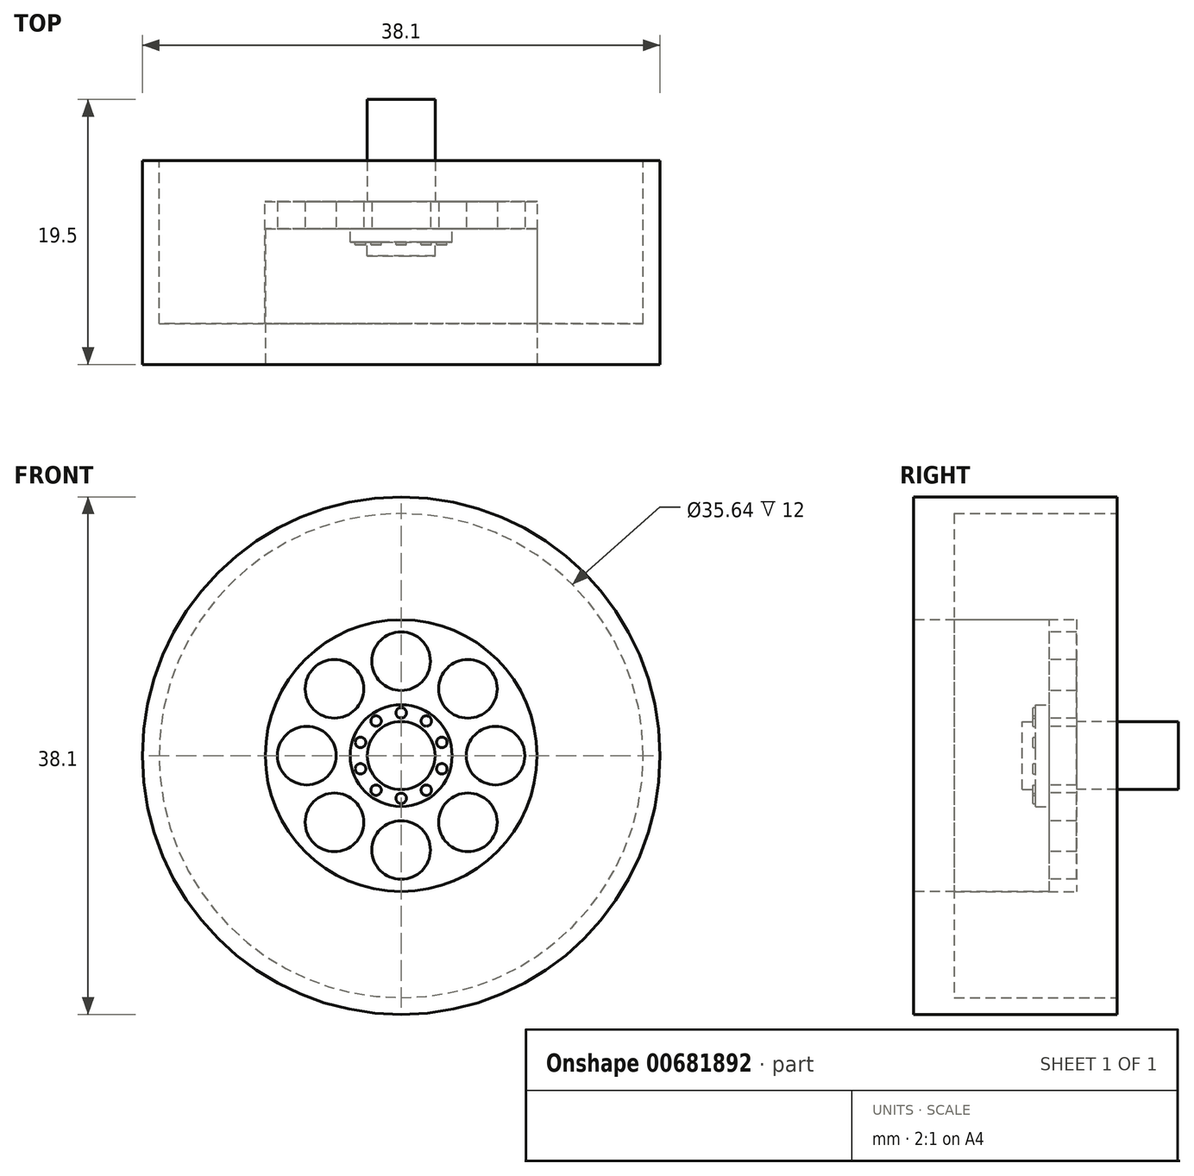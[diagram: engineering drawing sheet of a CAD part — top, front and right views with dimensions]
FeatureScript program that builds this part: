
annotation { "Feature Type Name" : "Feature", "Feature Type Description" : "" }
export const myFeature = defineFeature(function(context is Context, id is Id, definition is map)
    precondition{}
    {
        {
            var Q0;
            Q0=qCreatedBy(makeId("Front.planeOp"),FACE);
            var sketch = newSketch(context, id + "F0", { "sketchPlane" : qUnion([Q0])});
            skCircle(sketch, "E0", {"center": v(0, 0) * mm, "radius": 19.05 * mm});
            skSolve(sketch);
        }
        {
            var Q0;
            Q0=makeQuery(id+"F0.imprint","IMPRINT",FACE,{"disambiguationData":[TD([[makeQuery(id+"F0.imprint","IMPRINT",EDGE,{"derivedFrom":sQuery(id+"F0.wireOp",EDGE,"E0")}),1.0]])]});
            extrude(context, id + "F1", {"entities" : qUnion([Q0]), "depth" : 15 * mm, "offsetDistance" : 25.4 * mm});
        }
        {
            var Q0;
            Q0=makeQuery(id+"F1.opExtrude","CAP_FACE",FACE,{"disambiguationData":[OSD([sQuery(id+"F0.wireOp",EDGE,"E0")])],"isStart":false});
            var sketch = newSketch(context, id + "F2", { "sketchPlane" : qUnion([Q0])});
            skCircle(sketch, "E1", {"center": v(0, 0) * mm, "radius": 10 * mm});
            skSolve(sketch);
        }
        {
            var Q0;
            Q0=makeQuery(id+"F2.imprint","IMPRINT",FACE,{"disambiguationData":[TD([[makeQuery(id+"F2.imprint","IMPRINT",EDGE,{"derivedFrom":sQuery(id+"F2.wireOp",EDGE,"E1")}),1.0]])]});
            extrude(context, id + "F3", {"entities" : qUnion([Q0]), "operationType" : NewBodyOperationType.REMOVE, "oppositeDirection" : true, "depth" : 10 * mm, "offsetDistance" : 25.4 * mm});
        }
        {
            var Q0;
            Q0=makeQuery(id+"F3.boolean.opBoolean","COPY",FACE,{"derivedFrom":makeQuery(id+"F3.opExtrude","CAP_FACE",FACE,{"disambiguationData":[OSD([sQuery(id+"F2.wireOp",EDGE,"E1")])],"isStart":false})});
            var sketch = newSketch(context, id + "F4", { "sketchPlane" : qUnion([Q0])});
            skCircle(sketch, "E2", {"center": v(0, 0) * mm, "radius": 3.75 * mm});
            skSolve(sketch);
        }
        {
            var Q0;
            Q0=makeQuery(id+"F4.imprint","IMPRINT",FACE,{"disambiguationData":[TD([[makeQuery(id+"F4.imprint","IMPRINT",EDGE,{"derivedFrom":sQuery(id+"F4.wireOp",EDGE,"E2")}),1.0]])]});
            extrude(context, id + "F5", {"entities" : qUnion([Q0]), "operationType" : NewBodyOperationType.ADD, "depth" : 1 * mm, "offsetDistance" : 25.4 * mm});
        }
        {
            var Q0;
            Q0=makeQuery(id+"F5.opExtrude","CAP_FACE",FACE,{"disambiguationData":[OSD([sQuery(id+"F4.wireOp",EDGE,"E2")])],"isStart":false});
            var sketch = newSketch(context, id + "F6", { "sketchPlane" : qUnion([Q0])});
            skCircle(sketch, "E3", {"center": v(0, 0) * mm, "radius": 2.5 * mm});
            skSolve(sketch);
        }
        {
            var Q0;
            Q0=makeQuery(id+"F6.imprint","IMPRINT",FACE,{"disambiguationData":[TD([[makeQuery(id+"F6.imprint","IMPRINT",EDGE,{"derivedFrom":sQuery(id+"F6.wireOp",EDGE,"E3")}),1.0]])]});
            extrude(context, id + "F7", {"entities" : qUnion([Q0]), "operationType" : NewBodyOperationType.ADD, "depth" : 1 * mm, "offsetDistance" : 25.4 * mm});
        }
        {
            var Q0;
            Q0=makeQuery(id+"F3.boolean.opBoolean","COPY",FACE,{"derivedFrom":makeQuery(id+"F3.opExtrude","CAP_FACE",FACE,{"disambiguationData":[OSD([sQuery(id+"F2.wireOp",EDGE,"E1")])],"isStart":false})});
            var sketch = newSketch(context, id + "F8", { "sketchPlane" : qUnion([Q0])});
            skCircle(sketch, "E4", {"center": v(0, 6.95) * mm, "radius": 2.16 * mm});
            skCircle(sketch, "E5.1.0", {"center": v(-4.91, 4.91) * mm, "radius": 2.16 * mm});
            skCircle(sketch, "E5.2.0", {"center": v(-6.95, 0) * mm, "radius": 2.16 * mm});
            skCircle(sketch, "E5.3.0", {"center": v(-4.91, -4.91) * mm, "radius": 2.16 * mm});
            skCircle(sketch, "E5.4.0", {"center": v(0, -6.95) * mm, "radius": 2.16 * mm});
            skCircle(sketch, "E5.5.0", {"center": v(4.91, -4.91) * mm, "radius": 2.16 * mm});
            skCircle(sketch, "E5.6.0", {"center": v(6.95, 0) * mm, "radius": 2.16 * mm});
            skCircle(sketch, "E5.7.0", {"center": v(4.91, 4.91) * mm, "radius": 2.16 * mm});
            skPoint(sketch, "E5.center", {"position": v(0, 0) * mm});
            skSolve(sketch);
        }
        {
            var Q0;
            Q0=makeQuery(id+"F8.imprint","IMPRINT",FACE,{"disambiguationData":[TD([[makeQuery(id+"F8.imprint","IMPRINT",EDGE,{"derivedFrom":sQuery(id+"F8.wireOp",EDGE,"E4")}),1.0]])]});
            var Q1;
            Q1=makeQuery(id+"F8.imprint","IMPRINT",FACE,{"disambiguationData":[TD([[makeQuery(id+"F8.imprint","IMPRINT",EDGE,{"derivedFrom":sQuery(id+"F8.wireOp",EDGE,"E5.7.0")}),1.0]])]});
            var Q2;
            Q2=makeQuery(id+"F8.imprint","IMPRINT",FACE,{"disambiguationData":[TD([[makeQuery(id+"F8.imprint","IMPRINT",EDGE,{"derivedFrom":sQuery(id+"F8.wireOp",EDGE,"E5.6.0")}),1.0]])]});
            var Q3;
            Q3=makeQuery(id+"F8.imprint","IMPRINT",FACE,{"disambiguationData":[TD([[makeQuery(id+"F8.imprint","IMPRINT",EDGE,{"derivedFrom":sQuery(id+"F8.wireOp",EDGE,"E5.5.0")}),1.0]])]});
            var Q4;
            Q4=makeQuery(id+"F8.imprint","IMPRINT",FACE,{"disambiguationData":[TD([[makeQuery(id+"F8.imprint","IMPRINT",EDGE,{"derivedFrom":sQuery(id+"F8.wireOp",EDGE,"E5.4.0")}),1.0]])]});
            var Q5;
            Q5=makeQuery(id+"F8.imprint","IMPRINT",FACE,{"disambiguationData":[TD([[makeQuery(id+"F8.imprint","IMPRINT",EDGE,{"derivedFrom":sQuery(id+"F8.wireOp",EDGE,"E5.3.0")}),1.0]])]});
            var Q6;
            Q6=makeQuery(id+"F8.imprint","IMPRINT",FACE,{"disambiguationData":[TD([[makeQuery(id+"F8.imprint","IMPRINT",EDGE,{"derivedFrom":sQuery(id+"F8.wireOp",EDGE,"E5.2.0")}),1.0]])]});
            var Q7;
            Q7=makeQuery(id+"F8.imprint","IMPRINT",FACE,{"disambiguationData":[TD([[makeQuery(id+"F8.imprint","IMPRINT",EDGE,{"derivedFrom":sQuery(id+"F8.wireOp",EDGE,"E5.1.0")}),1.0]])]});
            extrude(context, id + "F9", {"entities" : qUnion([Q0, Q1, Q2, Q3, Q4, Q5, Q6, Q7]), "operationType" : NewBodyOperationType.REMOVE, "oppositeDirection" : true, "depth" : 18.8 * mm, "offsetDistance" : 25.4 * mm});
        }
        {
            var Q0;
            Q0=makeQuery(id+"F1.opExtrude","CAP_FACE",FACE,{"disambiguationData":[OSD([sQuery(id+"F0.wireOp",EDGE,"E0")])],"isStart":true});
            var sketch = newSketch(context, id + "F10", { "sketchPlane" : qUnion([Q0])});
            skCircle(sketch, "E6", {"center": v(0, 0) * mm, "radius": 17.5 * mm});
            skSolve(sketch);
        }
        {
            var Q0;
            Q0=makeQuery(id+"F10.imprint","IMPRINT",FACE,{"disambiguationData":[TD([[makeQuery(id+"F10.imprint","IMPRINT",EDGE,{"derivedFrom":sQuery(id+"F10.wireOp",EDGE,"E6")}),1.0]])]});
            extrude(context, id + "F11", {"entities" : qUnion([Q0]), "operationType" : NewBodyOperationType.REMOVE, "oppositeDirection" : true, "depth" : 3 * mm, "offsetDistance" : 25.4 * mm});
        }
        {
            var Q0;
            Q0=makeQuery(id+"F11.boolean.opBoolean","COPY",FACE,{"derivedFrom":makeQuery(id+"F11.opExtrude","CAP_FACE",FACE,{"disambiguationData":[OSD([sQuery(id+"F0.wireOp",EDGE,"E0"),sQuery(id+"F8.wireOp",EDGE,"E4"),sQuery(id+"F8.wireOp",EDGE,"E5.1.0"),sQuery(id+"F8.wireOp",EDGE,"E5.2.0"),sQuery(id+"F8.wireOp",EDGE,"E5.3.0"),sQuery(id+"F8.wireOp",EDGE,"E5.4.0"),sQuery(id+"F8.wireOp",EDGE,"E5.5.0"),sQuery(id+"F8.wireOp",EDGE,"E5.6.0"),sQuery(id+"F8.wireOp",EDGE,"E5.7.0"),sQuery(id+"F10.wireOp",EDGE,"E6")])],"isStart":false})});
            var sketch = newSketch(context, id + "F12", { "sketchPlane" : qUnion([Q0])});
            skCircle(sketch, "E7", {"center": v(0, 0) * mm, "radius": 2.5 * mm});
            skSolve(sketch);
        }
        {
            var Q0;
            Q0=makeQuery(id+"F5.opExtrude","CAP_FACE",FACE,{"disambiguationData":[OSD([sQuery(id+"F4.wireOp",EDGE,"E2")])],"isStart":false});
            var sketch = newSketch(context, id + "F13", { "sketchPlane" : qUnion([Q0])});
            skCircle(sketch, "E8", {"center": v(0, 3.15) * mm, "radius": 0.39 * mm});
            skCircle(sketch, "E9.1.0", {"center": v(-1.85, 2.55) * mm, "radius": 0.39 * mm});
            skCircle(sketch, "E9.2.0", {"center": v(-3, 0.97) * mm, "radius": 0.39 * mm});
            skCircle(sketch, "E9.3.0", {"center": v(-3, -0.97) * mm, "radius": 0.39 * mm});
            skCircle(sketch, "E9.4.0", {"center": v(-1.85, -2.55) * mm, "radius": 0.39 * mm});
            skCircle(sketch, "E9.5.0", {"center": v(0, -3.15) * mm, "radius": 0.39 * mm});
            skCircle(sketch, "E9.6.0", {"center": v(1.85, -2.55) * mm, "radius": 0.39 * mm});
            skCircle(sketch, "E9.7.0", {"center": v(3, -0.97) * mm, "radius": 0.39 * mm});
            skCircle(sketch, "E9.8.0", {"center": v(3, 0.97) * mm, "radius": 0.39 * mm});
            skCircle(sketch, "E9.9.0", {"center": v(1.85, 2.55) * mm, "radius": 0.39 * mm});
            skPoint(sketch, "E9.center", {"position": v(0, 0) * mm});
            skSolve(sketch);
        }
        {
            var Q0;
            Q0=makeQuery(id+"F13.imprint","IMPRINT",FACE,{"disambiguationData":[TD([[makeQuery(id+"F13.imprint","IMPRINT",EDGE,{"derivedFrom":sQuery(id+"F13.wireOp",EDGE,"E8")}),1.0]])]});
            var Q1;
            Q1=makeQuery(id+"F13.imprint","IMPRINT",FACE,{"disambiguationData":[TD([[makeQuery(id+"F13.imprint","IMPRINT",EDGE,{"derivedFrom":sQuery(id+"F13.wireOp",EDGE,"E9.9.0")}),1.0]])]});
            var Q2;
            Q2=makeQuery(id+"F13.imprint","IMPRINT",FACE,{"disambiguationData":[TD([[makeQuery(id+"F13.imprint","IMPRINT",EDGE,{"derivedFrom":sQuery(id+"F13.wireOp",EDGE,"E9.8.0")}),1.0]])]});
            var Q3;
            Q3=makeQuery(id+"F13.imprint","IMPRINT",FACE,{"disambiguationData":[TD([[makeQuery(id+"F13.imprint","IMPRINT",EDGE,{"derivedFrom":sQuery(id+"F13.wireOp",EDGE,"E9.7.0")}),1.0]])]});
            var Q4;
            Q4=makeQuery(id+"F13.imprint","IMPRINT",FACE,{"disambiguationData":[TD([[makeQuery(id+"F13.imprint","IMPRINT",EDGE,{"derivedFrom":sQuery(id+"F13.wireOp",EDGE,"E9.6.0")}),1.0]])]});
            var Q5;
            Q5=makeQuery(id+"F13.imprint","IMPRINT",FACE,{"disambiguationData":[TD([[makeQuery(id+"F13.imprint","IMPRINT",EDGE,{"derivedFrom":sQuery(id+"F13.wireOp",EDGE,"E9.5.0")}),1.0]])]});
            var Q6;
            Q6=makeQuery(id+"F13.imprint","IMPRINT",FACE,{"disambiguationData":[TD([[makeQuery(id+"F13.imprint","IMPRINT",EDGE,{"derivedFrom":sQuery(id+"F13.wireOp",EDGE,"E9.4.0")}),1.0]])]});
            var Q7;
            Q7=makeQuery(id+"F13.imprint","IMPRINT",FACE,{"disambiguationData":[TD([[makeQuery(id+"F13.imprint","IMPRINT",EDGE,{"derivedFrom":sQuery(id+"F13.wireOp",EDGE,"E9.3.0")}),1.0]])]});
            var Q8;
            Q8=makeQuery(id+"F13.imprint","IMPRINT",FACE,{"disambiguationData":[TD([[makeQuery(id+"F13.imprint","IMPRINT",EDGE,{"derivedFrom":sQuery(id+"F13.wireOp",EDGE,"E9.2.0")}),1.0]])]});
            var Q9;
            Q9=makeQuery(id+"F13.imprint","IMPRINT",FACE,{"disambiguationData":[TD([[makeQuery(id+"F13.imprint","IMPRINT",EDGE,{"derivedFrom":sQuery(id+"F13.wireOp",EDGE,"E9.1.0")}),1.0]])]});
            extrude(context, id + "F14", {"entities" : qUnion([Q0, Q1, Q2, Q3, Q4, Q5, Q6, Q7, Q8, Q9]), "operationType" : NewBodyOperationType.ADD, "depth" : 0.2 * mm, "offsetDistance" : 25.4 * mm});
        }
        {
            var Q0;
            Q0=makeQuery(id+"F12.imprint","IMPRINT",FACE,{"disambiguationData":[TD([[makeQuery(id+"F12.imprint","IMPRINT",EDGE,{"derivedFrom":sQuery(id+"F12.wireOp",EDGE,"E7")}),-1.0]])]});
            var sketch = newSketch(context, id + "F15", { "sketchPlane" : qUnion([Q0])});
            skCircle(sketch, "E10", {"center": v(0, 0) * mm, "radius": 10.03 * mm});
            skSolve(sketch);
        }
        {
            var Q0;
            Q0=makeQuery(id+"F15.imprint","IMPRINT",FACE,{"disambiguationData":[TD([[makeQuery(id+"F15.imprint","IMPRINT",EDGE,{"derivedFrom":sQuery(id+"F15.wireOp",EDGE,"E10")}),-1.0]])]});
            extrude(context, id + "F16", {"entities" : qUnion([Q0]), "operationType" : NewBodyOperationType.ADD, "depth" : 3 * mm, "offsetDistance" : 25.4 * mm});
        }
        {
            var Q0;
            Q0=makeQuery(id+"F16.boolean.opBoolean","MERGE",FACE,{"derivedFrom":[makeQuery(id+"F1.opExtrude","CAP_FACE",FACE,{"disambiguationData":[OSD([sQuery(id+"F0.wireOp",EDGE,"E0")])],"isStart":true}),makeQuery(id+"F16.opExtrude","CAP_FACE",FACE,{"disambiguationData":[OSD([sQuery(id+"F10.wireOp",EDGE,"E6"),sQuery(id+"F15.wireOp",EDGE,"E10")])],"isStart":false})]});
            var sketch = newSketch(context, id + "F17", { "sketchPlane" : qUnion([Q0])});
            skCircle(sketch, "E11", {"center": v(0, 0) * mm, "radius": 17.82 * mm});
            skSolve(sketch);
        }
        {
            var Q0;
            Q0=makeQuery(id+"F17.imprint","IMPRINT",FACE,{"disambiguationData":[TD([[makeQuery(id+"F17.imprint","IMPRINT",EDGE,{"derivedFrom":sQuery(id+"F17.wireOp",EDGE,"E11")}),1.0]])]});
            extrude(context, id + "F18", {"entities" : qUnion([Q0]), "operationType" : NewBodyOperationType.REMOVE, "oppositeDirection" : true, "depth" : 12 * mm, "offsetDistance" : 25.4 * mm});
        }
        {
            var Q0;
            Q0=makeQuery(id+"F12.imprint","IMPRINT",FACE,{"disambiguationData":[TD([[makeQuery(id+"F12.imprint","IMPRINT",EDGE,{"derivedFrom":sQuery(id+"F12.wireOp",EDGE,"E7")}),1.0]])]});
            extrude(context, id + "F19", {"entities" : qUnion([Q0]), "operationType" : NewBodyOperationType.ADD, "depth" : 7.5 * mm, "offsetDistance" : 25.4 * mm});
        }
    });
